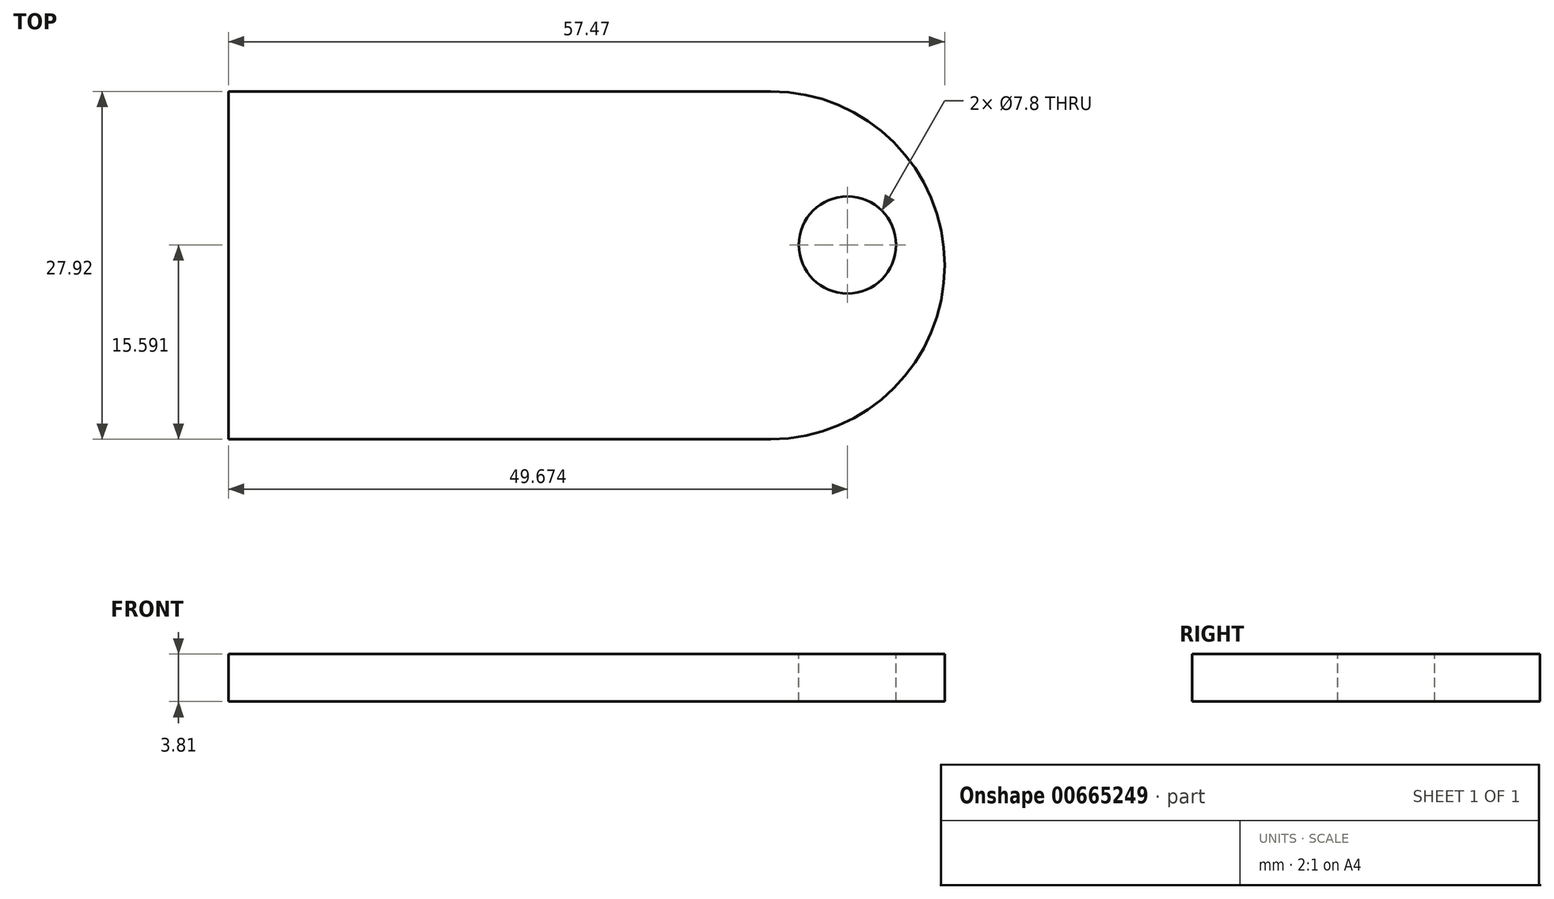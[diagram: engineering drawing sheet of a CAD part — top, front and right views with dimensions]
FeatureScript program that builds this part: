
annotation { "Feature Type Name" : "Feature", "Feature Type Description" : "" }
export const myFeature = defineFeature(function(context is Context, id is Id, definition is map)
    precondition{}
    {
        {
            var Q0;
            Q0=qCreatedBy(makeId("Top.planeOp"),FACE);
            var sketch = newSketch(context, id + "F0", { "sketchPlane" : qUnion([Q0])});
            skLineSegment(sketch, "E0.bottom", {"start": v(0, 0) * mm, "end": v(-43.5, 0) * mm});
            skLineSegment(sketch, "E0.top", {"start": v(0, 27.92) * mm, "end": v(-43.5, 27.92) * mm});
            skLineSegment(sketch, "E0.right", {"start": v(-43.5, 0) * mm, "end": v(-43.5, 27.92) * mm});
            skArc(sketch, "E1", {"start": v(0, 0) * mm, "mid": v(13.96, 13.96) * mm, "end": v(0, 27.92) * mm});
            skSolve(sketch);
        }
        {
            var Q0;
            Q0=makeQuery(id+"F0.imprint","IMPRINT",FACE,{"disambiguationData":[TD([[makeQuery(id+"F0.imprint","IMPRINT",EDGE,{"derivedFrom":sQuery(id+"F0.wireOp",EDGE,"E0.bottom")}),-1.0]])]});
            extrude(context, id + "F1", {"entities" : qUnion([Q0]), "depth" : 3.8 * mm, "offsetDistance" : 25.4 * mm});
        }
        {
            var Q0;
            Q0=makeQuery(id+"F1.opExtrude","CAP_FACE",FACE,{"disambiguationData":[OSD([sQuery(id+"F0.wireOp",EDGE,"E0.bottom"),sQuery(id+"F0.wireOp",EDGE,"E0.top"),sQuery(id+"F0.wireOp",EDGE,"E0.right"),sQuery(id+"F0.wireOp",EDGE,"E1")])],"isStart":false});
            var sketch = newSketch(context, id + "F2", { "sketchPlane" : qUnion([Q0])});
            skCircle(sketch, "E2", {"center": v(6.16, 15.6) * mm, "radius": 3.9 * mm});
            skSolve(sketch);
        }
        {
            var Q0;
            Q0=makeQuery(id+"F2.imprint","IMPRINT",FACE,{"disambiguationData":[TD([[makeQuery(id+"F2.imprint","IMPRINT",EDGE,{"derivedFrom":sQuery(id+"F2.wireOp",EDGE,"E2")}),1.0]])]});
            extrude(context, id + "F3", {"entities" : qUnion([Q0]), "operationType" : NewBodyOperationType.REMOVE, "oppositeDirection" : true, "depth" : 25.4 * mm, "offsetDistance" : 25.4 * mm});
        }
    });
